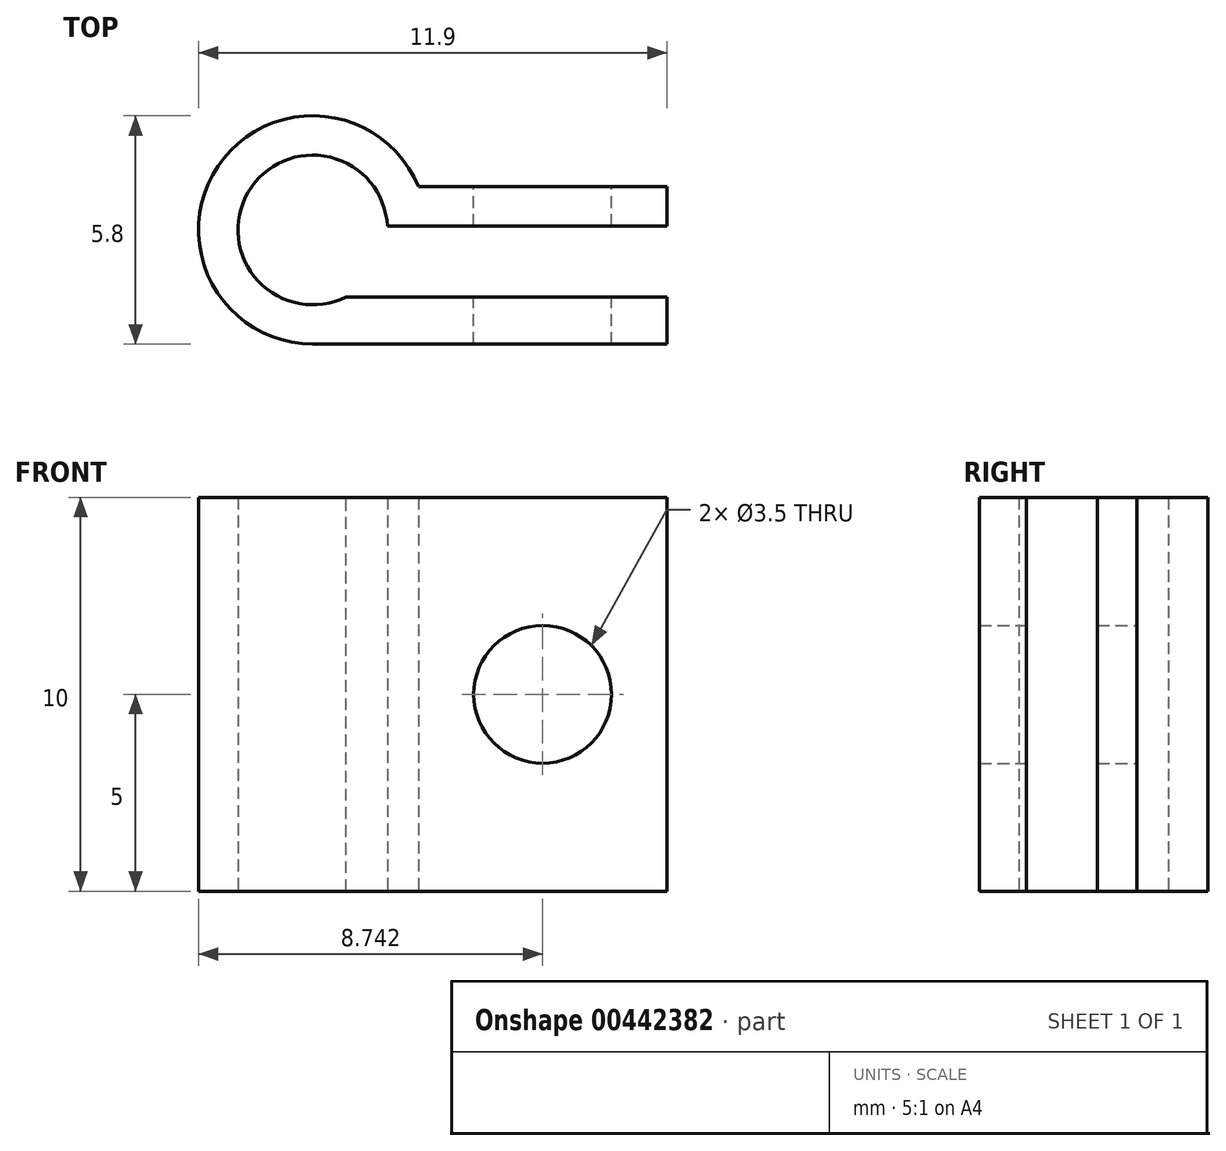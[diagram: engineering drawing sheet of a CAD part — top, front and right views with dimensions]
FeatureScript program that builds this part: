
annotation { "Feature Type Name" : "Feature", "Feature Type Description" : "" }
export const myFeature = defineFeature(function(context is Context, id is Id, definition is map)
    precondition{}
    {
        {
            var Q0;
            Q0=qCreatedBy(makeId("Top.planeOp"),FACE);
            var sketch = newSketch(context, id + "F0", { "sketchPlane" : qUnion([Q0])});
            skCircle(sketch, "E0", {"center": v(0, 0) * mm, "radius": 1.9 * mm});
            skCircle(sketch, "E1.0", {"center": v(0, 0) * mm, "radius": 2.9 * mm});
            skLineSegment(sketch, "E2", {"start": v(0, -2.9) * mm, "end": v(9, -2.9) * mm});
            skLineSegment(sketch, "E3", {"start": v(9, -2.9) * mm, "end": v(9, 1.1) * mm});
            skLineSegment(sketch, "E4", {"start": v(9, 1.1) * mm, "end": v(2.68, 1.1) * mm});
            skSolve(sketch);
        }
        {
            var Q0;
            Q0 = qSketchRegion(id + "F0", true);
            extrude(context, id + "F1", {"entities" : qUnion([Q0]), "depth" : 10 * mm, "offsetDistance" : 25 * mm});
        }
        {
            var Q0;
            Q0=makeQuery(id+"F1.opExtrude","CAP_FACE",FACE,{"disambiguationData":[OSD([sQuery(id+"F0.wireOp",EDGE,"E0"),sQuery(id+"F0.wireOp",EDGE,"E1.0"),sQuery(id+"F0.wireOp",EDGE,"E2"),sQuery(id+"F0.wireOp",EDGE,"E3"),sQuery(id+"F0.wireOp",EDGE,"E4")])],"isStart":false});
            var sketch = newSketch(context, id + "F2", { "sketchPlane" : qUnion([Q0])});
            skLineSegment(sketch, "E5.bottom", {"start": v(9, 0.1) * mm, "end": v(0.85, 0.1) * mm});
            skLineSegment(sketch, "E5.top", {"start": v(9, -1.7) * mm, "end": v(0.85, -1.7) * mm});
            skLineSegment(sketch, "E5.left", {"start": v(9, 0.1) * mm, "end": v(9, -1.7) * mm});
            skLineSegment(sketch, "E5.right", {"start": v(0.85, 0.1) * mm, "end": v(0.85, -1.7) * mm});
            skSolve(sketch);
        }
        {
            var Q0;
            Q0 = qSketchRegion(id + "F2", true);
            extrude(context, id + "F3", {"entities" : qUnion([Q0]), "operationType" : NewBodyOperationType.REMOVE, "oppositeDirection" : true, "depth" : 25 * mm, "offsetDistance" : 25 * mm});
        }
        {
            var Q0;
            Q0=makeQuery(id+"F1.opExtrude","SWEPT_FACE",FACE,{"disambiguationData":[OSD([sQuery(id+"F0.wireOp",EDGE,"E4")])]});
            var sketch = newSketch(context, id + "F4", { "sketchPlane" : qUnion([Q0])});
            skCircle(sketch, "E6", {"center": v(-5.84, 5) * mm, "radius": 1.75 * mm});
            skPoint(sketch, "E6.centerSnap0", {"position": v(-5.84, 10) * mm});
            skPoint(sketch, "E6.centerSnap1", {"position": v(-9, 5) * mm});
            skSolve(sketch);
        }
        {
            var Q0;
            Q0 = qSketchRegion(id + "F4", true);
            extrude(context, id + "F5", {"entities" : qUnion([Q0]), "operationType" : NewBodyOperationType.REMOVE, "oppositeDirection" : true, "depth" : 25 * mm, "offsetDistance" : 25 * mm});
        }
    });
